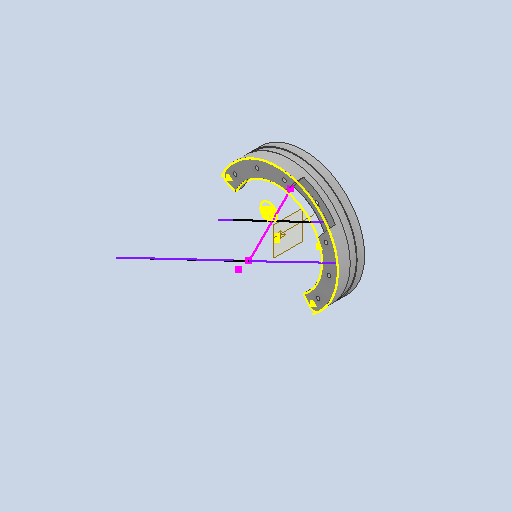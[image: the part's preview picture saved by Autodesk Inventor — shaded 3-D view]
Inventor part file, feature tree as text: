
AUTODESK INVENTOR PART (.ipt)
format: ipt  version: 2022 (Build 260153000, 153)  size: 310,272 bytes
history: native  units: in
note: dims shown in document units (in); Inventor stores cm internally (conversion verified against a paired STEP export)
features: other x10, reference x9, sketch x5, plane x3, extrude x2, projected_geometry x2, revolve x1, fillet x1, hole x1, pattern_circular x1
ambient origin geometry x8: Origin, YZ Plane, XZ Plane, XY Plane, X Axis, Y Axis, Z Axis, Center Point
bodies: Body1 (feature_tree)
feature tree (35):
  other  "Arbeitsachse1"
  plane  "Arbeitsebene4"
  revolve  "Umdrehung1"
  extrude  "Extrusion9"  Depth=0.1969in
  fillet  "Rundung2"  [1 undecoded]
  sketch  "Skizze13"  dims[d41=0.2362in]
  plane  "Arbeitsebene6"
  hole  "Bohrung1"  [1 undecoded]
  pattern_circular  "Runde Anordnung1"  Angle=360.0deg  [1 undecoded]
  sketch  "Skizze17"  dims[d43=0.0236in d44=360.0deg d46=0.3937in d47=0.0in d55=0.1969in d56=0.0118in d68=105.0deg d69=105.0deg d70=0.1102in d71=0.1102in d72=0.2362in d73=0.1969in d74=0.3937in d75=90.0deg d76=0.315in d77=0.8108in d78=4.7244in d79=360.0deg d81=0.1181in d82=0.3937in d83=0.0in]
  other  "Arbeitspunkt2"
  extrude  "Extrusion14"  Depth=0.3937in TaperAngle=0.0deg
  plane  "Arbeitsebene3"
  other  "Arbeitspunkt1"
  sketch  "Skizze10"  dims[d36=0.1575in d37=0.1969in d38=135.0deg]
  reference  "Referenz27"
  reference  "Referenz28"
  sketch  "Skizze11"  dims[d39=0.0118in d40=0.0984in]
  reference  "Referenz29"
  reference  "Referenz30"
  reference  "Referenz31"
  projected_geometry  "Projizierte Kontur8"
  projected_geometry  "Projizierte Kontur9"
  reference  "Referenz37"
  reference  "Referenz38"
  reference  "Referenz39"
  sketch  "Skizze16"  dims[d42=0.4724in]
  reference  "Referenz40"
  other  "Anglerfish_bonne_mamman_m12large_flipped_v0.iam"
  other  "00_Lid_Bonne_Mamman:1"
  other  "00_Coverglass:1"
  other  "Anglerfish_Lightplate_Tosslink:1"
  other  "Matchboxscope_M12_Lensadapter_v0:1"
  other  "00_toslink_launcher_v3:2"
  other  "00_toslink_launcher_v3:1"
note: 3 required parameter values undecoded (feature->parameter linkage not recoverable at this tier; creation-order binding heuristic only, values carry confidence <= 0.55)
